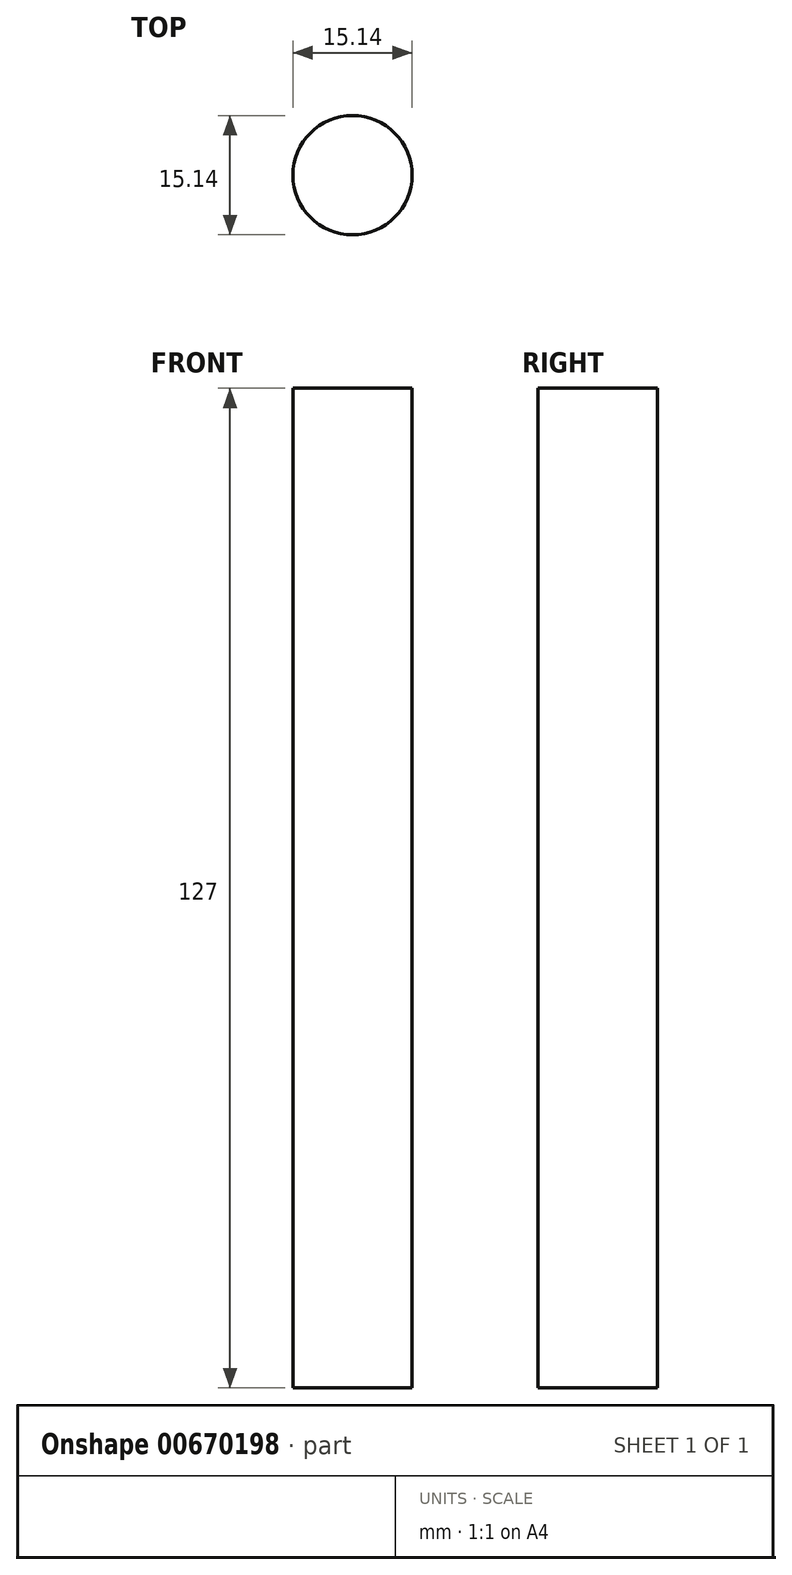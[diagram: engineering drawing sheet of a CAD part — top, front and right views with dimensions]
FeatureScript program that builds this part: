
annotation { "Feature Type Name" : "Feature", "Feature Type Description" : "" }
export const myFeature = defineFeature(function(context is Context, id is Id, definition is map)
    precondition{}
    {
        {
            var Q0;
            Q0=qCreatedBy(makeId("Top.planeOp"),FACE);
            var sketch = newSketch(context, id + "F0", { "sketchPlane" : qUnion([Q0])});
            skCircle(sketch, "E0", {"center": v(0, 0) * mm, "radius": 7.57 * mm});
            skSolve(sketch);
        }
        {
            var Q0;
            Q0 = qSketchRegion(id + "F0", true);
            extrude(context, id + "F1", {"entities" : qUnion([Q0]), "depth" : 127 * mm, "offsetDistance" : 25.4 * mm});
        }
    });
